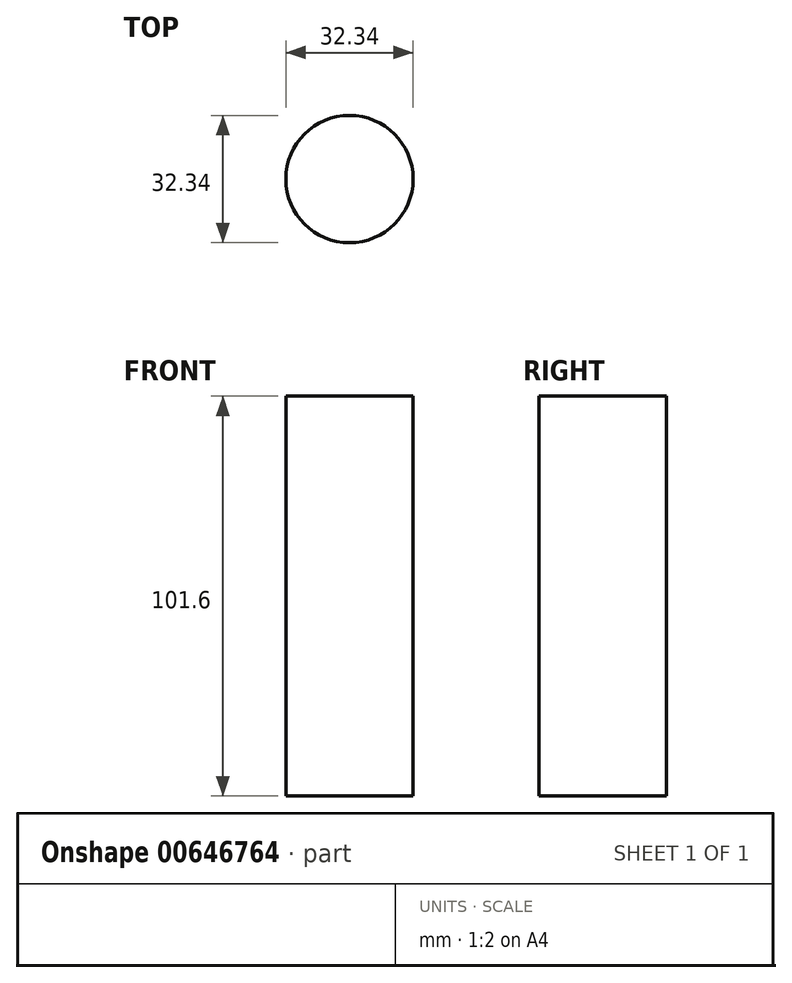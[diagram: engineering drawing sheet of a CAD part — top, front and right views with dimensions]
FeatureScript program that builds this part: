
annotation { "Feature Type Name" : "Feature", "Feature Type Description" : "" }
export const myFeature = defineFeature(function(context is Context, id is Id, definition is map)
    precondition{}
    {
        {
            var Q0;
            Q0=qCreatedBy(makeId("Top.planeOp"),FACE);
            var sketch = newSketch(context, id + "F0", { "sketchPlane" : qUnion([Q0])});
            skCircle(sketch, "E0", {"center": v(0, 0) * mm, "radius": 16.17 * mm});
            skSolve(sketch);
        }
        {
            var Q0;
            Q0 = qSketchRegion(id + "F0", true);
            extrude(context, id + "F1", {"entities" : qUnion([Q0]), "depth" : 101.6 * mm, "offsetDistance" : 25.4 * mm});
        }
    });
